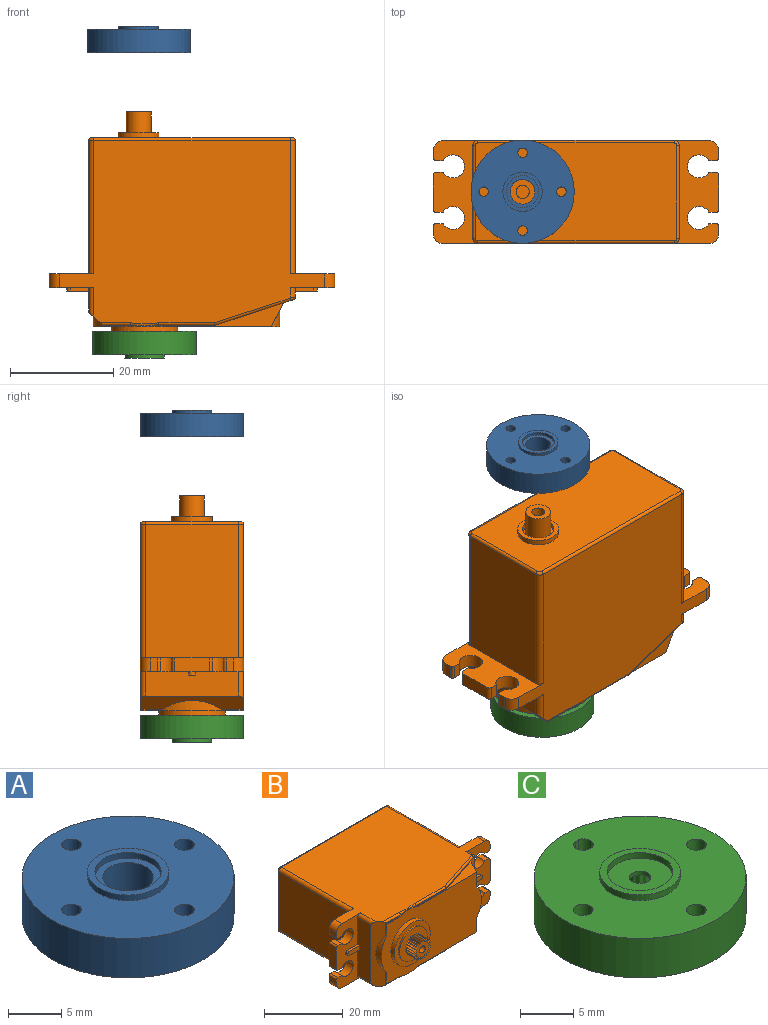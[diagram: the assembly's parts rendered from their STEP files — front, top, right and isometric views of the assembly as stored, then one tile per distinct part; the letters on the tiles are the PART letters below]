
ASSEMBLY  parts=3 mates=3
PART A: 37 faces, bbox 20x20x5.2 mm
  f0: plane 6.25x6.25mm, normal (0,0,1), area 12.6mm2, adj f31,f34
  f1: plane 20x20mm, normal (0,0,-1), area 132.5mm2, adj f2,f4,f9,f13,f15,f16,f23,f24
  f2: cylinder r=10mm len=20mm, axis (0,0,-1), area 285.9mm2, adj f1,f3
  f3: plane 20x20mm, normal (0,0,1), area 257.4mm2, adj f2,f28,f29,f30,f32,f35
  f4: cylinder r=8.45mm len=5.73mm, axis (0,0,-1), area 21.1mm2, adj f1,f8,f9,f23
  f5: plane 1.9x1.19mm, normal (1,0,0), area 2.3mm2, adj f6,f8,f23,f33
  f6: cylinder r=3.95mm len=3.47mm, axis (0,0,-1), area 10.1mm2, adj f5,f7,f8,f33
  f7: plane 1.9x1.19mm, normal (0,-1,0), area 2.3mm2, adj f6,f8,f9,f33
  f8: plane 7.66x7.66mm, normal (0,0,-1), area 29.4mm2, adj f4,f5,f6,f7,f9,f23
  f9: cylinder r=2.45mm len=4.9mm, axis (0,0,-1), area 20.5mm2, adj f1,f4,f7,f8,f10,f13,f14,f33
  f10: plane 1.9x1.19mm, normal (0,1,0), area 2.3mm2, adj f9,f11,f14,f33
  f11: cylinder r=3.95mm len=3.47mm, axis (0,0,-1), area 10.1mm2, adj f10,f12,f14,f33
  f12: plane 1.9x1.19mm, normal (1,0,0), area 2.3mm2, adj f11,f14,f16,f33
  f13: cylinder r=8.45mm len=5.73mm, axis (0,0,-1), area 21.1mm2, adj f1,f9,f14,f16
  f14: plane 7.66x7.66mm, normal (0,0,-1), area 29.4mm2, adj f9,f10,f11,f12,f13,f16
  f15: cylinder r=8.45mm len=5.73mm, axis (0,0,-1), area 21.1mm2, adj f1,f16,f20,f25
  f16: cylinder r=2.45mm len=4.9mm, axis (0,0,-1), area 20.5mm2, adj f1,f12,f13,f14,f15,f17,f20,f33
  f17: plane 1.9x1.19mm, normal (-1,0,0), area 2.3mm2, adj f16,f18,f20,f33
  f18: cylinder r=3.95mm len=3.47mm, axis (0,0,-1), area 10.1mm2, adj f17,f19,f20,f33
  f19: plane 1.9x1.19mm, normal (0,1,0), area 2.3mm2, adj f18,f20,f25,f33
  f20: plane 7.66x7.66mm, normal (0,0,-1), area 29.4mm2, adj f15,f16,f17,f18,f19,f25
  f21: cylinder r=3.95mm len=3.47mm, axis (0,0,-1), area 10.1mm2, adj f22,f26,f27,f33
  f22: plane 1.9x1.19mm, normal (-1,0,0), area 2.3mm2, adj f21,f23,f27,f33
  f23: cylinder r=2.45mm len=4.9mm, axis (0,0,-1), area 20.5mm2, adj f1,f4,f5,f8,f22,f24,f27,f33
  f24: cylinder r=8.45mm len=5.73mm, axis (0,0,-1), area 21.1mm2, adj f1,f23,f25,f27
  f25: cylinder r=2.45mm len=4.9mm, axis (0,0,-1), area 20.5mm2, adj f1,f15,f19,f20,f24,f26,f27,f33
  f26: plane 1.9x1.19mm, normal (0,-1,0), area 2.3mm2, adj f21,f25,f27,f33
  f27: plane 7.66x7.66mm, normal (0,0,-1), area 29.4mm2, adj f21,f22,f23,f24,f25,f26
  f28: cylinder r=0.93mm len=4.55mm, axis (0,0,-1), area 26.4mm2, adj f1,f3
  f29: cylinder r=0.93mm len=4.55mm, axis (0,0,-1), area 26.4mm2, adj f1,f3
  f30: cylinder r=0.93mm len=4.55mm, axis (0,0,-1), area 26.4mm2, adj f1,f3
  f31: cylinder r=2.4mm len=4.8mm, axis (0,0,-1), area 59.6mm2, adj f0,f33
  f32: cylinder r=0.93mm len=4.55mm, axis (0,0,-1), area 26.4mm2, adj f1,f3
  f33: plane 10.23x10.23mm, normal (0,0,-1), area 35.1mm2, adj f5,f6,f7,f9,f10,f11,f12,f16
  f34: cylinder r=3.12mm len=6.25mm, axis (0,0,-1), area 12.8mm2, adj f0,f36
  f35: cylinder r=3.82mm len=7.65mm, axis (0,0,-1), area 15.6mm2, adj f3,f36
  f36: plane 7.65x7.65mm, normal (0,0,1), area 15.3mm2, adj f34,f35
PART B: 184 faces, bbox 55.7x47x20.6 mm
  f0: plane 5.31x0.2mm, normal (0,-1,0), area 1mm2, adj f7,f38,f54,f166
  f1: plane 10.84x0.2mm, normal (0,-1,0), area 2.1mm2, adj f9,f41,f53,f169
  f2: plane 9.95x9.95mm, normal (0,-1,0), area 56.7mm2, adj f58,f59,f60,f61,f62,f63,f64,f65
  f3: plane 23.52x4.6mm, normal (0,0,-1), area 29.3mm2, adj f10,f40,f41,f43,f54
  f4: plane 4.71x0.25mm, normal (0,0,1), area 1.2mm2, adj f5,f10,f42,f53
  f5: plane 3.61x0.25mm, normal (-1,0,0), area 0.9mm2, adj f4,f10,f38,f55
  f6: plane 18x4.75mm, normal (-1,0,0), area 84.5mm2, adj f20,f38,f49,f51,f52,f157,f158
  f7: plane 4.71x0.25mm, normal (0,0,-1), area 1.2mm2, adj f0,f10,f39,f54
  f8: plane 18x1.89mm, normal (1,0,0), area 33mm2, adj f18,f45,f46,f48,f159,f160,f175
  f9: plane 23.52x4.6mm, normal (0,0,1), area 29.3mm2, adj f1,f10,f41,f43,f53
  f10: plane 36.09x19.8mm, normal (0,-1,0), area 506.1mm2, adj f3,f4,f5,f7,f9,f39,f43,f44
  f11: plane 51.3x35.55mm, normal (0,0,1), area 1343.2mm2, adj f17,f18,f19,f20,f38,f146,f147,f157
  f12: plane 51.3x35.55mm, normal (0,0,-1), area 1343.2mm2, adj f17,f18,f19,f20,f38,f145,f148,f158
  f13: plane 6.75x2.64mm, normal (1,0,0), area 17.8mm2, adj f17,f18,f149,f151
  f14: plane 2.64x1.38mm, normal (1,0,0), area 3.6mm2, adj f17,f18,f148,f152
  f15: plane 6.75x2.64mm, normal (-1,0,0), area 17.8mm2, adj f19,f20,f154,f155
  f16: plane 2.64x1.38mm, normal (-1,0,0), area 3.6mm2, adj f19,f20,f146,f156
  f17: plane 20x8.65mm, normal (0,1,0), area 112.7mm2, adj f11,f12,f13,f14,f21,f24,f32,f33
  f18: plane 20x8.65mm, normal (0,-1,0), area 107.2mm2, adj f8,f11,f12,f13,f14,f24,f32,f33
  f19: plane 20x8.65mm, normal (0,1,0), area 112.7mm2, adj f11,f12,f15,f16,f23,f25,f26,f27
  f20: plane 20x8.65mm, normal (0,-1,0), area 107.2mm2, adj f6,f11,f12,f15,f16,f25,f26,f27
  f21: plane 25.86x18mm, normal (1,0,0), area 465.5mm2, adj f17,f161,f163,f181
  f22: plane 39x19mm, normal (0,1,0), area 692.1mm2, adj f138,f176,f177,f178,f179,f180,f181,f182
  f23: plane 25.86x18mm, normal (-1,0,0), area 465.5mm2, adj f19,f162,f164,f178
  f24: plane 2.64x1.38mm, normal (1,0,0), area 3.6mm2, adj f17,f18,f147,f150
  f25: plane 2.64x1.38mm, normal (-1,0,0), area 3.6mm2, adj f19,f20,f145,f153
  f26: cylinder r=2.23mm len=4.45mm, axis (0,-1,0), area 30.7mm2, adj f19,f20,f27,f28
  f27: plane 2.64x1.41mm, normal (0,0,-1), area 3.7mm2, adj f19,f20,f26,f156
  f28: plane 2.64x1.41mm, normal (0,0,1), area 3.7mm2, adj f19,f20,f26,f155
  f29: cylinder r=2.23mm len=4.45mm, axis (0,-1,0), area 30.7mm2, adj f19,f20,f30,f31
  f30: plane 2.64x1.41mm, normal (0,0,-1), area 3.7mm2, adj f19,f20,f29,f154
  f31: plane 2.64x1.41mm, normal (0,0,1), area 3.7mm2, adj f19,f20,f29,f153
  f32: plane 2.64x1.41mm, normal (0,0,-1), area 3.7mm2, adj f17,f18,f34,f151
  f33: plane 2.64x1.41mm, normal (0,0,1), area 3.7mm2, adj f17,f18,f34,f152
  f34: cylinder r=2.23mm len=4.45mm, axis (0,-1,0), area 30.7mm2, adj f17,f18,f32,f33
  f35: plane 2.64x1.41mm, normal (0,0,1), area 3.7mm2, adj f17,f18,f37,f149
  f36: plane 2.64x1.41mm, normal (0,0,-1), area 3.7mm2, adj f17,f18,f37,f150
  f37: cylinder r=2.23mm len=4.45mm, axis (0,-1,0), area 30.7mm2, adj f17,f18,f35,f36
  f38: plane 20.4x3.11mm, normal (-0.69,-0.72,0), area 54.9mm2, adj f0,f5,f6,f11,f12,f39,f42,f55
  f39: plane 3.61x0.25mm, normal (-1,0,0), area 0.9mm2, adj f7,f10,f38,f55
  f40: plane 10.84x0.2mm, normal (0,-1,0), area 2.1mm2, adj f3,f41,f54,f170
  f41: plane 19x15.23mm, normal (0.31,-0.95,0), area 44.2mm2, adj f1,f3,f9,f40,f43,f171,f172,f173
  f42: plane 5.31x0.2mm, normal (0,-1,0), area 1mm2, adj f4,f38,f53,f165
  f43: plane 18.6x4.6mm, normal (0.89,-0.46,0), area 73.4mm2, adj f3,f9,f10,f41,f44
  f44: cylinder r=7.47mm len=9.4mm, axis (0,-1,0), area 21.5mm2, adj f10,f43
  f45: plane 3.61x0.71mm, normal (0,0,1), area 2.6mm2, adj f8,f18,f47,f48
  f46: plane 3.61x0.71mm, normal (0,0,-1), area 2.6mm2, adj f8,f18,f47,f48
  f47: cylinder r=0.68mm len=1.35mm, axis (0,1,0), area 1.5mm2, adj f18,f45,f46,f48
  f48: plane 4.28x1.35mm, normal (0,-1,0), area 5.6mm2, adj f8,f45,f46,f47
  f49: plane 3.61x0.71mm, normal (0,0,1), area 2.6mm2, adj f6,f20,f50,f52
  f50: cylinder r=0.68mm len=1.35mm, axis (0,1,0), area 1.5mm2, adj f20,f49,f51,f52
  f51: plane 3.61x0.71mm, normal (0,0,-1), area 2.6mm2, adj f6,f20,f50,f52
  f52: plane 4.28x1.35mm, normal (0,-1,0), area 5.6mm2, adj f6,f49,f50,f51
  f53: cylinder r=9.9mm len=6.79mm, axis (0,-1,0), area 1.7mm2, adj f1,f4,f9,f10,f42,f167
  f54: cylinder r=9.9mm len=6.79mm, axis (0,-1,0), area 1.7mm2, adj f0,f3,f7,f10,f40,f168
  f55: cylinder r=9.9mm len=11.38mm, axis (0,-1,0), area 16.9mm2, adj f5,f10,f38,f39
  f56: cylinder r=6.45mm len=12.9mm, axis (0,1,0), area 51.5mm2, adj f10,f57
  f57: plane 12.9x12.9mm, normal (0,-1,0), area 52.9mm2, adj f56,f58
  f58: cylinder r=4.98mm len=9.95mm, axis (0,1,0), area 11.9mm2, adj f2,f57
  f59: plane 3.3x0.69mm, normal (0.96,0,0.27), area 2.3mm2, adj f2,f60,f134,f135
  f60: cylinder r=2.92mm len=3.3mm, axis (0,1,0), area 0.1mm2, adj f2,f59,f61,f135
  f61: plane 3.3x0.62mm, normal (-0.87,0,0.5), area 2.3mm2, adj f2,f60,f62,f135
  f62: plane 3.3x0.62mm, normal (0.87,0,0.5), area 2.3mm2, adj f2,f61,f63,f135
  f63: cylinder r=2.92mm len=3.3mm, axis (0,1,0), area 0.1mm2, adj f2,f62,f64,f135
  f64: plane 3.3x0.69mm, normal (-0.96,0,0.27), area 2.3mm2, adj f2,f63,f65,f135
  f65: plane 3.3x0.51mm, normal (0.71,0,0.7), area 2.3mm2, adj f2,f64,f66,f135
  f66: cylinder r=2.92mm len=3.3mm, axis (0,1,0), area 0.1mm2, adj f2,f65,f67,f135
  f67: plane 3.3x0.71mm, normal (-1,0,0.02), area 2.3mm2, adj f2,f66,f68,f135
  f68: plane 3.3x0.61mm, normal (0.52,0,0.86), area 2.3mm2, adj f2,f67,f69,f135
  f69: cylinder r=2.92mm len=3.3mm, axis (0,1,0), area 0.1mm2, adj f2,f68,f70,f135
  f70: plane 3.3x0.69mm, normal (-0.97,0,-0.23), area 2.3mm2, adj f2,f69,f71,f135
  f71: plane 3.3x0.68mm, normal (0.29,0,0.96), area 2.3mm2, adj f2,f70,f72,f135
  f72: cylinder r=2.92mm len=3.3mm, axis (0,1,0), area 0.1mm2, adj f2,f71,f73,f135
  f73: plane 3.3x0.63mm, normal (-0.89,0,-0.46), area 2.3mm2, adj f2,f72,f74,f135
  f74: plane 3.3x0.71mm, normal (0.04,0,1), area 2.3mm2, adj f2,f73,f75,f135
  f75: cylinder r=2.92mm len=3.3mm, axis (0,1,0), area 0.1mm2, adj f2,f74,f76,f135
  f76: plane 3.3x0.53mm, normal (-0.74,0,-0.67), area 2.3mm2, adj f2,f75,f77,f135
  f77: plane 3.3x0.7mm, normal (-0.21,0,0.98), area 2.3mm2, adj f2,f76,f78,f135
  f78: cylinder r=2.92mm len=3.3mm, axis (0,1,0), area 0.1mm2, adj f2,f77,f79,f135
  f79: plane 3.3x0.59mm, normal (-0.55,0,-0.83), area 2.3mm2, adj f2,f78,f80,f135
  f80: plane 3.3x0.64mm, normal (-0.44,0,0.9), area 2.3mm2, adj f2,f79,f81,f135
  f81: cylinder r=2.92mm len=3.3mm, axis (0,1,0), area 0.1mm2, adj f2,f80,f82,f135
  f82: plane 3.3x0.67mm, normal (-0.33,0,-0.94), area 2.3mm2, adj f2,f81,f83,f135
  f83: plane 3.3x0.54mm, normal (-0.65,0,0.76), area 2.3mm2, adj f2,f82,f84,f135
  f84: cylinder r=2.92mm len=3.3mm, axis (0,1,0), area 0.1mm2, adj f2,f83,f85,f135
  f85: plane 3.3x0.71mm, normal (-0.08,0,-1), area 2.3mm2, adj f2,f84,f86,f135
  f86: plane 3.3x0.58mm, normal (-0.82,0,0.57), area 2.3mm2, adj f2,f85,f87,f135
  f87: cylinder r=2.92mm len=3.3mm, axis (0,1,0), area 0.1mm2, adj f2,f86,f88,f135
  f88: plane 3.3x0.7mm, normal (0.17,0,-0.99), area 2.3mm2, adj f2,f87,f89,f135
  f89: plane 3.3x0.67mm, normal (-0.94,0,0.35), area 2.3mm2, adj f2,f88,f90,f135
  f90: cylinder r=2.92mm len=3.3mm, axis (0,1,0), area 0.1mm2, adj f2,f89,f91,f135
  f91: plane 3.3x0.65mm, normal (0.41,0,-0.91), area 2.3mm2, adj f2,f90,f92,f135
  f92: plane 3.3x0.71mm, normal (-0.99,0,0.1), area 2.3mm2, adj f2,f91,f93,f135
  f93: cylinder r=2.92mm len=3.3mm, axis (0,1,0), area 0.1mm2, adj f2,f92,f94,f135
  f94: plane 3.3x0.56mm, normal (0.62,0,-0.78), area 2.3mm2, adj f2,f93,f95,f135
  f95: plane 3.3x0.7mm, normal (-0.99,0,-0.15), area 2.3mm2, adj f2,f94,f96,f135
  f96: cylinder r=2.92mm len=3.3mm, axis (0,1,0), area 0.1mm2, adj f2,f95,f97,f135
  f97: plane 3.3x0.57mm, normal (0.8,0,-0.6), area 2.3mm2, adj f2,f96,f98,f135
  f98: plane 3.3x0.66mm, normal (-0.92,0,-0.39), area 2.3mm2, adj f2,f97,f99,f135
  f99: cylinder r=2.92mm len=3.3mm, axis (0,1,0), area 0.1mm2, adj f2,f98,f100,f135
  f100: plane 3.3x0.66mm, normal (0.92,0,-0.39), area 2.3mm2, adj f2,f99,f101,f135
  f101: plane 3.3x0.57mm, normal (-0.8,0,-0.6), area 2.3mm2, adj f2,f100,f102,f135
  f102: cylinder r=2.92mm len=3.3mm, axis (0,1,0), area 0.1mm2, adj f2,f101,f103,f135
  f103: plane 3.3x0.7mm, normal (0.99,0,-0.15), area 2.3mm2, adj f2,f102,f104,f135
  f104: plane 3.3x0.56mm, normal (-0.62,0,-0.78), area 2.3mm2, adj f2,f103,f105,f135
  f105: cylinder r=2.92mm len=3.3mm, axis (0,1,0), area 0.1mm2, adj f2,f104,f106,f135
  f106: plane 3.3x0.71mm, normal (0.99,0,0.1), area 2.3mm2, adj f2,f105,f107,f135
  f107: plane 3.3x0.65mm, normal (-0.41,0,-0.91), area 2.3mm2, adj f2,f106,f108,f135
  f108: cylinder r=2.92mm len=3.3mm, axis (0,1,0), area 0.1mm2, adj f2,f107,f109,f135
  f109: plane 3.3x0.67mm, normal (0.94,0,0.35), area 2.3mm2, adj f2,f108,f110,f135
  f110: plane 3.3x0.7mm, normal (-0.17,0,-0.99), area 2.3mm2, adj f2,f109,f111,f135
  f111: cylinder r=2.92mm len=3.3mm, axis (0,1,0), area 0.1mm2, adj f2,f110,f112,f135
  f112: plane 3.3x0.58mm, normal (0.82,0,0.57), area 2.3mm2, adj f2,f111,f113,f135
  f113: plane 3.3x0.71mm, normal (0.08,0,-1), area 2.3mm2, adj f2,f112,f114,f135
  f114: cylinder r=2.92mm len=3.3mm, axis (0,1,0), area 0.1mm2, adj f2,f113,f115,f135
  f115: plane 3.3x0.54mm, normal (0.65,0,0.76), area 2.3mm2, adj f2,f114,f116,f135
  f116: plane 3.3x0.67mm, normal (0.33,0,-0.94), area 2.3mm2, adj f2,f115,f117,f135
  f117: cylinder r=2.92mm len=3.3mm, axis (0,1,0), area 0.1mm2, adj f2,f116,f118,f135
  f118: plane 3.3x0.64mm, normal (0.44,0,0.9), area 2.3mm2, adj f2,f117,f119,f135
  f119: plane 3.3x0.59mm, normal (0.55,0,-0.83), area 2.3mm2, adj f2,f118,f120,f135
  f120: cylinder r=2.92mm len=3.3mm, axis (0,1,0), area 0.1mm2, adj f2,f119,f121,f135
  f121: plane 3.3x0.7mm, normal (0.21,0,0.98), area 2.3mm2, adj f2,f120,f122,f135
  f122: plane 3.3x0.53mm, normal (0.74,0,-0.67), area 2.3mm2, adj f2,f121,f123,f135
  f123: cylinder r=2.92mm len=3.3mm, axis (0,1,0), area 0.1mm2, adj f2,f122,f124,f135
  f124: plane 3.3x0.71mm, normal (-0.04,0,1), area 2.3mm2, adj f2,f123,f125,f135
  f125: plane 3.3x0.63mm, normal (0.89,0,-0.46), area 2.3mm2, adj f2,f124,f126,f135
  f126: cylinder r=2.92mm len=3.3mm, axis (0,1,0), area 0.1mm2, adj f2,f125,f127,f135
  f127: plane 3.3x0.68mm, normal (-0.29,0,0.96), area 2.3mm2, adj f2,f126,f128,f135
  f128: plane 3.3x0.69mm, normal (0.97,0,-0.23), area 2.3mm2, adj f2,f127,f129,f135
  f129: cylinder r=2.92mm len=3.3mm, axis (0,1,0), area 0.1mm2, adj f2,f128,f130,f135
  f130: plane 3.3x0.61mm, normal (-0.52,0,0.86), area 2.3mm2, adj f2,f129,f131,f135
  f131: plane 3.3x0.71mm, normal (1,0,0.02), area 2.3mm2, adj f2,f130,f132,f135
  f132: cylinder r=2.92mm len=3.3mm, axis (0,1,0), area 0.1mm2, adj f2,f131,f134,f135
  f133: cylinder r=1.02mm len=3.3mm, axis (0,1,0), area 21.1mm2, adj f135,f136
  f134: plane 3.3x0.51mm, normal (-0.71,0,0.7), area 2.3mm2, adj f2,f59,f132,f135
  f135: plane 5.83x5.82mm, normal (0,-1,0), area 17.8mm2, adj f59,f60,f61,f62,f63,f64,f65,f66
  f136: plane 2.03x2.03mm, normal (0,-1,0), area 3.2mm2, adj f133
  f137: cylinder r=3.05mm len=6.1mm, axis (0,-1,0), area 18.7mm2, adj f139,f140
  f138: cylinder r=3.94mm len=7.87mm, axis (0,-1,0), area 24.2mm2, adj f22,f139
  f139: plane 7.87x7.87mm, normal (0,1,0), area 19.5mm2, adj f137,f138
  f140: plane 6.1x6.1mm, normal (0,1,0), area 10.9mm2, adj f137,f142
  f141: cylinder r=1.27mm len=5.03mm, axis (0,-1,0), area 40.1mm2, adj f143,f144
  f142: cylinder r=2.41mm len=5.03mm, axis (0,-1,0), area 76.2mm2, adj f140,f143
  f143: plane 4.83x4.83mm, normal (0,1,0), area 13.2mm2, adj f141,f142
  f144: plane 2.54x2.54mm, normal (0,1,0), area 5.1mm2, adj f141
  f145: cylinder r=2mm len=2.64mm, axis (0,1,0), area 8.3mm2, adj f12,f19,f20,f25
  f146: cylinder r=2mm len=2.64mm, axis (0,-1,0), area 8.3mm2, adj f11,f16,f19,f20
  f147: cylinder r=2mm len=2.64mm, axis (0,-1,0), area 8.3mm2, adj f11,f17,f18,f24
  f148: cylinder r=2mm len=2.64mm, axis (0,1,0), area 8.3mm2, adj f12,f14,f17,f18
  f149: cylinder r=0.5mm len=2.64mm, axis (0,-1,0), area 2.1mm2, adj f13,f17,f18,f35
  f150: cylinder r=0.5mm len=2.64mm, axis (0,1,0), area 2.1mm2, adj f17,f18,f24,f36
  f151: cylinder r=0.5mm len=2.64mm, axis (0,1,0), area 2.1mm2, adj f13,f17,f18,f32
  f152: cylinder r=0.5mm len=2.64mm, axis (0,-1,0), area 2.1mm2, adj f14,f17,f18,f33
  f153: cylinder r=0.5mm len=2.64mm, axis (0,1,0), area 2.1mm2, adj f19,f20,f25,f31
  f154: cylinder r=0.5mm len=2.64mm, axis (0,-1,0), area 2.1mm2, adj f15,f19,f20,f30
  f155: cylinder r=0.5mm len=2.64mm, axis (0,1,0), area 2.1mm2, adj f15,f19,f20,f28
  f156: cylinder r=0.5mm len=2.64mm, axis (0,1,0), area 2.1mm2, adj f16,f19,f20,f27
  f157: cylinder r=1mm len=5.71mm, axis (0,1,0), area 8.2mm2, adj f6,f11,f20,f38
  f158: cylinder r=1mm len=5.71mm, axis (0,-1,0), area 8.2mm2, adj f6,f12,f20,f38
  f159: cylinder r=1mm len=2.05mm, axis (0,-1,0), area 3.1mm2, adj f8,f11,f18,f173
  f160: cylinder r=1mm len=2.05mm, axis (0,1,0), area 3.1mm2, adj f8,f12,f18,f174
  f161: cylinder r=1mm len=25.86mm, axis (0,1,0), area 40.6mm2, adj f12,f17,f21,f183
  f162: cylinder r=1mm len=25.86mm, axis (0,-1,0), area 40.6mm2, adj f12,f19,f23,f180
  f163: cylinder r=1mm len=25.86mm, axis (0,-1,0), area 40.6mm2, adj f11,f17,f21,f179
  f164: cylinder r=1mm len=25.86mm, axis (0,1,0), area 40.6mm2, adj f11,f19,f23,f176
  f165: cylinder r=0.5mm len=5.83mm, axis (1,0,0), area 4.4mm2, adj f11,f38,f42,f167
  f166: cylinder r=0.5mm len=5.83mm, axis (1,0,0), area 4.4mm2, adj f0,f12,f38,f168
  f167: bspline ~5.91x0.57mm, area 2.7mm2, adj f11,f53,f165,f169
  f168: bspline ~5.91x0.57mm, area 2.7mm2, adj f12,f54,f166,f170
  f169: cylinder r=0.5mm len=10.84mm, axis (1,0,0), area 8.5mm2, adj f1,f11,f167,f171
  f170: cylinder r=0.5mm len=10.84mm, axis (1,0,0), area 8.5mm2, adj f12,f40,f168,f172
  f171: cylinder r=0.5mm len=14.89mm, axis (-0.95,-0.31,0), area 12.1mm2, adj f11,f41,f169,f173
  f172: cylinder r=0.5mm len=14.89mm, axis (0.95,0.31,0), area 12.1mm2, adj f12,f41,f170,f174
  f173: bspline ~1.19x1.17mm, area 0.8mm2, adj f41,f159,f171,f175
  f174: bspline ~1.1x1.01mm, area 0.8mm2, adj f41,f160,f172,f175
  f175: cylinder r=0.5mm len=18mm, axis (0,0,-1), area 11.3mm2, adj f8,f41,f173,f174
  f176: torus R=0.5mm, axis (0,-1,0), area 1mm2, adj f22,f164,f177,f178
  f177: cylinder r=0.5mm len=38mm, axis (1,0,0), area 29.8mm2, adj f11,f22,f176,f179
  f178: cylinder r=0.5mm len=18mm, axis (0,0,-1), area 14.1mm2, adj f22,f23,f176,f180
  f179: torus R=0.5mm, axis (0,-1,0), area 1mm2, adj f22,f163,f177,f181
  f180: torus R=0.5mm, axis (0,-1,0), area 1mm2, adj f22,f162,f178,f182
  f181: cylinder r=0.5mm len=18mm, axis (0,0,1), area 14.1mm2, adj f21,f22,f179,f183
  f182: cylinder r=0.5mm len=38mm, axis (-1,0,0), area 29.8mm2, adj f12,f22,f180,f183
  f183: torus R=0.5mm, axis (0,-1,0), area 1mm2, adj f22,f161,f181,f182
PART C: 118 faces, bbox 20x20x5.2 mm
  f0: plane 6.2x6.2mm, normal (0,0,1), area 26.9mm2, adj f38,f115
  f1: plane 20x20mm, normal (0,0,-1), area 131.4mm2, adj f2,f7,f11,f14,f15,f16,f21,f22
  f2: cylinder r=10mm len=20mm, axis (0,0,-1), area 285.9mm2, adj f1,f3
  f3: plane 20x20mm, normal (0,0,1), area 258.1mm2, adj f2,f21,f22,f30,f31,f32,f33,f34
  f4: plane 2.7x1.22mm, normal (0,1,0), area 3.3mm2, adj f5,f8,f14,f35
  f5: cylinder r=3.95mm len=3.47mm, axis (0,0,-1), area 14.3mm2, adj f4,f6,f8,f35
  f6: plane 2.7x1.24mm, normal (1,0,0), area 3.4mm2, adj f5,f8,f25,f35
  f7: cylinder r=8.45mm len=5.76mm, axis (0,0,-1), area 25.5mm2, adj f1,f8,f14,f25
  f8: plane 7.67x7.66mm, normal (0,0,-1), area 29.7mm2, adj f4,f5,f6,f7,f14,f25
  f9: cylinder r=3.95mm len=3.5mm, axis (0,0,-1), area 14.4mm2, adj f10,f12,f13,f35
  f10: plane 2.7x1.21mm, normal (-1,0,0), area 3.3mm2, adj f9,f13,f16,f35
  f11: cylinder r=8.45mm len=5.78mm, axis (0,0,-1), area 25.5mm2, adj f1,f13,f16,f23
  f12: plane 2.7x1.24mm, normal (0,-1,0), area 3.3mm2, adj f9,f13,f23,f35
  f13: plane 7.68x7.67mm, normal (0,0,-1), area 29.7mm2, adj f9,f10,f11,f12,f16,f23
  f14: cylinder r=2.43mm len=4.85mm, axis (0,0,-1), area 24mm2, adj f1,f4,f7,f8,f15,f19,f20,f35
  f15: cylinder r=8.45mm len=5.79mm, axis (0,0,-1), area 25.6mm2, adj f1,f14,f16,f20
  f16: cylinder r=2.43mm len=4.85mm, axis (0,0,-1), area 24mm2, adj f1,f10,f11,f13,f15,f17,f20,f35
  f17: plane 2.7x1.22mm, normal (1,0,0), area 3.3mm2, adj f16,f18,f20,f35
  f18: cylinder r=3.95mm len=3.47mm, axis (0,0,-1), area 14.3mm2, adj f17,f19,f20,f35
  f19: plane 2.7x1.22mm, normal (0,-1,0), area 3.3mm2, adj f14,f18,f20,f35
  f20: plane 7.67x7.67mm, normal (0,0,-1), area 29.7mm2, adj f14,f15,f16,f17,f18,f19
  f21: cylinder r=0.93mm len=4.55mm, axis (0,0,-1), area 26.2mm2, adj f1,f3,f22
  f22: cylinder r=8.45mm len=4.55mm, axis (0,0,-1), area 0.3mm2, adj f1,f3,f21
  f23: cylinder r=2.43mm len=4.85mm, axis (0,0,-1), area 23.8mm2, adj f1,f11,f12,f13,f24,f28,f29,f35
  f24: cylinder r=8.45mm len=5.75mm, axis (0,0,-1), area 25.4mm2, adj f1,f23,f25,f29
  f25: cylinder r=2.43mm len=4.85mm, axis (0,0,-1), area 23.8mm2, adj f1,f6,f7,f8,f24,f26,f29,f35
  f26: plane 2.7x1.24mm, normal (-1,0,0), area 3.4mm2, adj f25,f27,f29,f35
  f27: cylinder r=3.95mm len=3.47mm, axis (0,0,-1), area 14.2mm2, adj f26,f28,f29,f35
  f28: plane 2.7x1.25mm, normal (0,1,0), area 3.4mm2, adj f23,f27,f29,f35
  f29: plane 7.66x7.64mm, normal (0,0,-1), area 29.6mm2, adj f23,f24,f25,f26,f27,f28
  f30: cylinder r=0.93mm len=4.55mm, axis (0,0,-1), area 24.4mm2, adj f1,f3,f31
  f31: cylinder r=8.45mm len=4.55mm, axis (0,0,-1), area 2.1mm2, adj f1,f3,f30
  f32: cylinder r=8.45mm len=4.55mm, axis (0,0,-1), area 2.1mm2, adj f1,f3,f33
  f33: cylinder r=0.93mm len=4.55mm, axis (0,0,-1), area 24.3mm2, adj f1,f3,f32
  f34: cylinder r=0.93mm len=4.55mm, axis (0,0,-1), area 26.4mm2, adj f1,f3
  f35: plane 10.31x10.31mm, normal (0,0,-1), area 13.7mm2, adj f4,f5,f6,f9,f10,f12,f14,f16
  f36: cylinder r=3.55mm len=7.1mm, axis (0,0,-1), area 11.2mm2, adj f35,f37
  f37: plane 7.1x7.1mm, normal (0,0,-1), area 18.5mm2, adj f36,f39,f40,f41,f42,f43,f44,f45
  f38: cylinder r=1.02mm len=2.03mm, axis (0,0,-1), area 2.9mm2, adj f0,f114
  f39: plane 3.3x0.51mm, normal (-0.71,-0.7,0), area 2.3mm2, adj f37,f40,f113,f114
  f40: plane 3.3x0.69mm, normal (0.96,-0.27,0), area 2.3mm2, adj f37,f39,f41,f114
  f41: cylinder r=2.92mm len=3.3mm, axis (0,0,-1), area 0.1mm2, adj f37,f40,f42,f114
  f42: plane 3.3x0.62mm, normal (-0.87,-0.5,0), area 2.3mm2, adj f37,f41,f43,f114
  f43: plane 3.3x0.62mm, normal (0.87,-0.5,0), area 2.3mm2, adj f37,f42,f44,f114
  f44: cylinder r=2.92mm len=3.3mm, axis (0,0,-1), area 0.1mm2, adj f37,f43,f45,f114
  f45: plane 3.3x0.69mm, normal (-0.96,-0.27,0), area 2.3mm2, adj f37,f44,f46,f114
  f46: plane 3.3x0.51mm, normal (0.71,-0.7,0), area 2.3mm2, adj f37,f45,f47,f114
  f47: cylinder r=2.92mm len=3.3mm, axis (0,0,-1), area 0.1mm2, adj f37,f46,f48,f114
  f48: plane 3.3x0.71mm, normal (-1,-0.02,0), area 2.3mm2, adj f37,f47,f49,f114
  f49: plane 3.3x0.61mm, normal (0.52,-0.86,0), area 2.3mm2, adj f37,f48,f50,f114
  f50: cylinder r=2.92mm len=3.3mm, axis (0,0,-1), area 0.1mm2, adj f37,f49,f51,f114
  f51: plane 3.3x0.69mm, normal (-0.97,0.23,0), area 2.3mm2, adj f37,f50,f52,f114
  f52: plane 3.3x0.68mm, normal (0.29,-0.96,0), area 2.3mm2, adj f37,f51,f53,f114
  f53: cylinder r=2.92mm len=3.3mm, axis (0,0,-1), area 0.1mm2, adj f37,f52,f54,f114
  f54: plane 3.3x0.63mm, normal (-0.89,0.46,0), area 2.3mm2, adj f37,f53,f55,f114
  f55: plane 3.3x0.71mm, normal (0.04,-1,0), area 2.3mm2, adj f37,f54,f56,f114
  f56: cylinder r=2.92mm len=3.3mm, axis (0,0,-1), area 0.1mm2, adj f37,f55,f57,f114
  f57: plane 3.3x0.53mm, normal (-0.74,0.67,0), area 2.3mm2, adj f37,f56,f58,f114
  f58: plane 3.3x0.7mm, normal (-0.21,-0.98,0), area 2.3mm2, adj f37,f57,f59,f114
  f59: cylinder r=2.92mm len=3.3mm, axis (0,0,-1), area 0.1mm2, adj f37,f58,f60,f114
  f60: plane 3.3x0.59mm, normal (-0.55,0.83,0), area 2.3mm2, adj f37,f59,f61,f114
  f61: plane 3.3x0.64mm, normal (-0.44,-0.9,0), area 2.3mm2, adj f37,f60,f62,f114
  f62: cylinder r=2.92mm len=3.3mm, axis (0,0,-1), area 0.1mm2, adj f37,f61,f63,f114
  f63: plane 3.3x0.67mm, normal (-0.33,0.94,0), area 2.3mm2, adj f37,f62,f64,f114
  f64: plane 3.3x0.54mm, normal (-0.65,-0.76,0), area 2.3mm2, adj f37,f63,f65,f114
  f65: cylinder r=2.92mm len=3.3mm, axis (0,0,-1), area 0.1mm2, adj f37,f64,f66,f114
  f66: plane 3.3x0.71mm, normal (-0.08,1,0), area 2.3mm2, adj f37,f65,f67,f114
  f67: plane 3.3x0.58mm, normal (-0.82,-0.57,0), area 2.3mm2, adj f37,f66,f68,f114
  f68: cylinder r=2.92mm len=3.3mm, axis (0,0,-1), area 0.1mm2, adj f37,f67,f69,f114
  f69: plane 3.3x0.7mm, normal (0.17,0.99,0), area 2.3mm2, adj f37,f68,f70,f114
  f70: plane 3.3x0.67mm, normal (-0.94,-0.35,0), area 2.3mm2, adj f37,f69,f71,f114
  f71: cylinder r=2.92mm len=3.3mm, axis (0,0,-1), area 0.1mm2, adj f37,f70,f72,f114
  f72: plane 3.3x0.65mm, normal (0.41,0.91,0), area 2.3mm2, adj f37,f71,f73,f114
  f73: plane 3.3x0.71mm, normal (-0.99,-0.1,0), area 2.3mm2, adj f37,f72,f74,f114
  f74: cylinder r=2.92mm len=3.3mm, axis (0,0,-1), area 0.1mm2, adj f37,f73,f75,f114
  f75: plane 3.3x0.56mm, normal (0.62,0.78,0), area 2.3mm2, adj f37,f74,f76,f114
  f76: plane 3.3x0.7mm, normal (-0.99,0.15,0), area 2.3mm2, adj f37,f75,f77,f114
  f77: cylinder r=2.92mm len=3.3mm, axis (0,0,-1), area 0.1mm2, adj f37,f76,f78,f114
  f78: plane 3.3x0.57mm, normal (0.8,0.6,0), area 2.3mm2, adj f37,f77,f79,f114
  f79: plane 3.3x0.66mm, normal (-0.92,0.39,0), area 2.3mm2, adj f37,f78,f80,f114
  f80: cylinder r=2.92mm len=3.3mm, axis (0,0,-1), area 0.1mm2, adj f37,f79,f81,f114
  f81: plane 3.3x0.66mm, normal (0.92,0.39,0), area 2.3mm2, adj f37,f80,f82,f114
  f82: plane 3.3x0.57mm, normal (-0.8,0.6,0), area 2.3mm2, adj f37,f81,f83,f114
  f83: cylinder r=2.92mm len=3.3mm, axis (0,0,-1), area 0.1mm2, adj f37,f82,f84,f114
  f84: plane 3.3x0.7mm, normal (0.99,0.15,0), area 2.3mm2, adj f37,f83,f85,f114
  f85: plane 3.3x0.56mm, normal (-0.62,0.78,0), area 2.3mm2, adj f37,f84,f86,f114
  f86: cylinder r=2.92mm len=3.3mm, axis (0,0,-1), area 0.1mm2, adj f37,f85,f87,f114
  f87: plane 3.3x0.71mm, normal (0.99,-0.1,0), area 2.3mm2, adj f37,f86,f88,f114
  f88: plane 3.3x0.65mm, normal (-0.41,0.91,0), area 2.3mm2, adj f37,f87,f89,f114
  f89: cylinder r=2.92mm len=3.3mm, axis (0,0,-1), area 0.1mm2, adj f37,f88,f90,f114
  f90: plane 3.3x0.67mm, normal (0.94,-0.35,0), area 2.3mm2, adj f37,f89,f91,f114
  f91: plane 3.3x0.7mm, normal (-0.17,0.99,0), area 2.3mm2, adj f37,f90,f92,f114
  f92: cylinder r=2.92mm len=3.3mm, axis (0,0,-1), area 0.1mm2, adj f37,f91,f93,f114
  f93: plane 3.3x0.58mm, normal (0.82,-0.57,0), area 2.3mm2, adj f37,f92,f94,f114
  f94: plane 3.3x0.71mm, normal (0.08,1,0), area 2.3mm2, adj f37,f93,f95,f114
  f95: cylinder r=2.92mm len=3.3mm, axis (0,0,-1), area 0.1mm2, adj f37,f94,f96,f114
  f96: plane 3.3x0.54mm, normal (0.65,-0.76,0), area 2.3mm2, adj f37,f95,f97,f114
  f97: plane 3.3x0.67mm, normal (0.33,0.94,0), area 2.3mm2, adj f37,f96,f98,f114
  f98: cylinder r=2.92mm len=3.3mm, axis (0,0,-1), area 0.1mm2, adj f37,f97,f99,f114
  f99: plane 3.3x0.64mm, normal (0.44,-0.9,0), area 2.3mm2, adj f37,f98,f100,f114
  f100: plane 3.3x0.59mm, normal (0.55,0.83,0), area 2.3mm2, adj f37,f99,f101,f114
  f101: cylinder r=2.92mm len=3.3mm, axis (0,0,-1), area 0.1mm2, adj f37,f100,f102,f114
  f102: plane 3.3x0.7mm, normal (0.21,-0.98,0), area 2.3mm2, adj f37,f101,f103,f114
  f103: plane 3.3x0.53mm, normal (0.74,0.67,0), area 2.3mm2, adj f37,f102,f104,f114
  f104: cylinder r=2.92mm len=3.3mm, axis (0,0,-1), area 0.1mm2, adj f37,f103,f105,f114
  f105: plane 3.3x0.71mm, normal (-0.04,-1,0), area 2.3mm2, adj f37,f104,f106,f114
  f106: plane 3.3x0.63mm, normal (0.89,0.46,0), area 2.3mm2, adj f37,f105,f107,f114
  f107: cylinder r=2.92mm len=3.3mm, axis (0,0,-1), area 0.1mm2, adj f37,f106,f108,f114
  f108: plane 3.3x0.68mm, normal (-0.29,-0.96,0), area 2.3mm2, adj f37,f107,f109,f114
  f109: plane 3.3x0.69mm, normal (0.97,0.23,0), area 2.3mm2, adj f37,f108,f110,f114
  f110: cylinder r=2.92mm len=3.3mm, axis (0,0,-1), area 0.1mm2, adj f37,f109,f111,f114
  f111: plane 3.3x0.61mm, normal (-0.52,-0.86,0), area 2.3mm2, adj f37,f110,f112,f114
  f112: plane 3.3x0.71mm, normal (1,-0.02,0), area 2.3mm2, adj f37,f111,f113,f114
  f113: cylinder r=2.92mm len=3.3mm, axis (0,0,-1), area 0.1mm2, adj f37,f39,f112,f114
  f114: plane 5.83x5.82mm, normal (0,0,-1), area 17.8mm2, adj f38,f39,f40,f41,f42,f43,f44,f45
  f115: cylinder r=3.1mm len=6.2mm, axis (0,0,-1), area 12.7mm2, adj f0,f117
  f116: cylinder r=3.8mm len=7.6mm, axis (0,0,-1), area 15.5mm2, adj f3,f117
  f117: plane 7.6x7.6mm, normal (0,0,1), area 15.2mm2, adj f115,f116
PLACE A t=(28.09,-2.73,30.37)mm
PLACE B rot(axis=(1,0,0),90deg) t=(38.43,7.27,-4.39)mm
PLACE C rot(axis=(1,0,0),180deg) t=(29.24,-2.73,-23.54)mm
MATE slider C.f2 <-> B.f53  axis (0,0,1) through (29.24,-2.73,-27.64)mm
MATE slider B.f137 <-> A.f2  axis (0,0,-1) through (28.09,-2.73,16.42)mm
MATE planar C.f2 <-> B.f53  axis (0,0,1) through (29.24,-2.73,-24.34)mm
